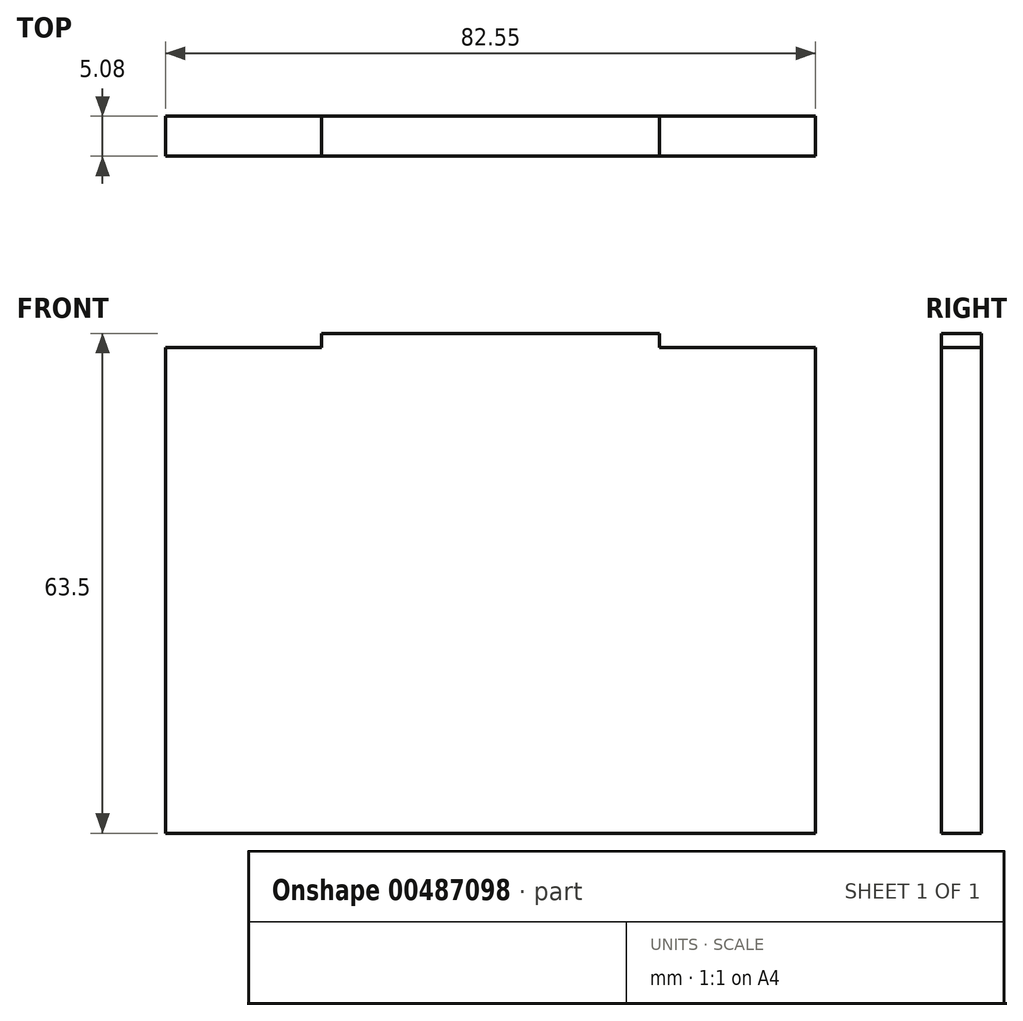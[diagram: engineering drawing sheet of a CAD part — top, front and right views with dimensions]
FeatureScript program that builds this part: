
annotation { "Feature Type Name" : "Feature", "Feature Type Description" : "" }
export const myFeature = defineFeature(function(context is Context, id is Id, definition is map)
    precondition{}
    {
        {
            var Q0;
            Q0=qCreatedBy(makeId("Front.planeOp"),FACE);
            var sketch = newSketch(context, id + "F0", { "sketchPlane" : qUnion([Q0])});
            skLineSegment(sketch, "E0.bottom", {"start": v(-22.46, 34.02) * mm, "end": v(20.47, 34.02) * mm});
            skLineSegment(sketch, "E0.top", {"start": v(-42.27, -29.48) * mm, "end": v(40.28, -29.48) * mm});
            skLineSegment(sketch, "E0.left", {"start": v(-42.27, 32.24) * mm, "end": v(-42.27, -29.48) * mm});
            skLineSegment(sketch, "E0.right", {"start": v(40.28, 32.24) * mm, "end": v(40.28, -29.48) * mm});
            skLineSegment(sketch, "E1.top", {"start": v(-42.27, 32.24) * mm, "end": v(-22.46, 32.24) * mm});
            skLineSegment(sketch, "E1.right", {"start": v(-22.46, 34.02) * mm, "end": v(-22.46, 32.24) * mm});
            skLineSegment(sketch, "E2.top", {"start": v(40.28, 32.24) * mm, "end": v(20.47, 32.24) * mm});
            skLineSegment(sketch, "E2.right", {"start": v(20.47, 34.02) * mm, "end": v(20.47, 32.24) * mm});
            skSolve(sketch);
        }
        {
            var Q0;
            Q0 = qSketchRegion(id + "F0", true);
            extrude(context, id + "F1", {"entities" : qUnion([Q0]), "depth" : 5.08 * mm});
        }
    });
